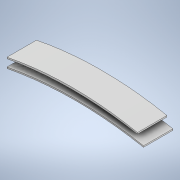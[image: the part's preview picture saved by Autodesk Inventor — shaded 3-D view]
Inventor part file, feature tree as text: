
AUTODESK INVENTOR PART (.ipt)
format: ipt  version: 2020.2 (Build 242310000, 310)  size: 112,640 bytes
history: native  units: mm
features: extrude x1, sketch x1
ambient origin geometry x8: Origin, YZ Plane, XZ Plane, XY Plane, X Axis, Y Axis, Z Axis, Center Point
bodies: Solide1 (feature_tree)
feature tree (2):
  extrude  "Extrusion1"  Depth=785.7mm
  sketch  "Esquisse1"
